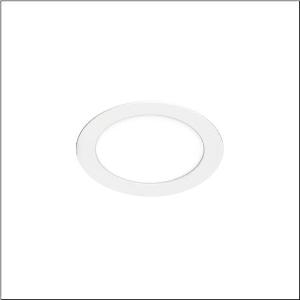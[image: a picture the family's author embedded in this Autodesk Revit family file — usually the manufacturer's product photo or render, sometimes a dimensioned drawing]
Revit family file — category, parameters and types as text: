
# Revit family: lunis_41_flat_51dr107fhca
name_source: partatom
category: Lighting Fixtures
units: mm (PartAtom-declared; Revit-internal decimal feet)

## family parameters
Cut with Voids When Loaded = No
Host = Face
Light Source = No
Part Type = Normal
Room Calculation Point = No
Round Connector Dimension = Use Diameter
Shared = No

## types (1)
- --- (1 x LED, 2160 lm, 22 W, 5700K)
    Apparent Load = 22 VA
    CIE Flux Codes = 49 80 96 100 100
    Color Rendering = 80
    Color Temperature = 5700K
    Default Elevation = 1800 mm
    Description = Lunis 41,  flat, downlight, light emission: direct distribution, LED rated luminous flux: 2.160lm, light colour: 840/857, control gear: ECG, mains connection: 230V, AC, 50/60Hz, housing, round, of aluminium, coated, traffic white (RAL 9016), diameter: 225mm, protection rating (complete): IP20, protection rating (on room side): IP44, insulation class (complete): insulation class II (safety insulation), certification: CE, permissible ambient temperature for indoor applications: -20..+40°C, packaging unit: 1 piece
    Height = 0 mm  [stored 0 ft]
    Lamp = 1 x LED
    Lamp Light Flux = 2160 lm
    Lamp Power = 22 W
    Lamp count = 1
    Length = 225 mm
    Luminous efficacy = 98 lm/W
    Manufacturer = Siteco
    ModVariant = No
    Model = 51DR107FHCA
    Mounting Place = Ceiling
    Mounting Type = Recessed
    Number of Poles = 1
    OnlyDefault = Yes
    Power Factor = 1
    Product Name = Lunis 41 flat
    Product group = downlight
    ProductGroupID = 400
    Protection Class = Protection class II
    Protection Degree = IP 20
    RLX_Detail_Level = 1
    RLX_Emergency_Light_Flux = 0 lm
    RLX_Emergency_Type = 0
    RLX_Emergency_Type_DB = No
    RlxData = <blob elided: 21985 chars, md5=59b7cfeb>
    Socket = socket
    Standby Power = 0 W
    System Light Flux = 2160 lm
    System Power = 22 W
    Type Comments = factory setting: colour temperature 5700K
    Type Image = l_1007032.jpg
    URL = http://relux.com
    VarID = @adj_130671
    Voltage = 0 V
    Weight = 0.00 kg
    Width = 0 mm  [stored 0 ft]

note: [stored X ft] marks values corroborated as IEEE doubles in the binary element streams (Revit-internal decimal feet)

## geometry (parser evidence)
native form markers: Blend x4, Sweep x11
no freeform markers — native parametric forms only
